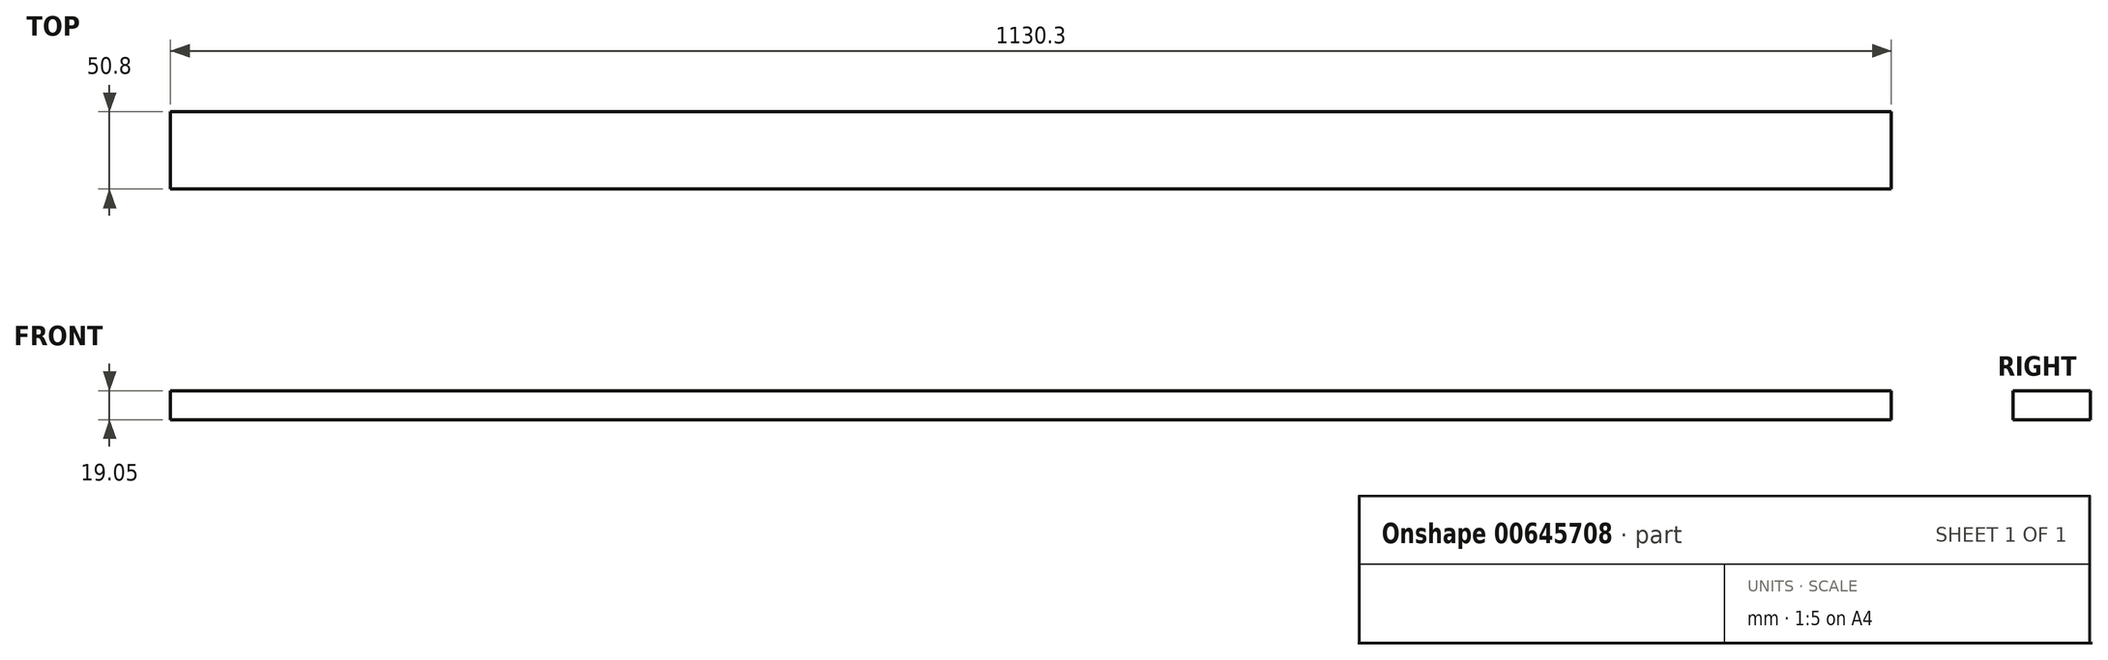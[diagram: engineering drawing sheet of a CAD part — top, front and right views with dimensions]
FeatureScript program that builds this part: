
annotation { "Feature Type Name" : "Feature", "Feature Type Description" : "" }
export const myFeature = defineFeature(function(context is Context, id is Id, definition is map)
    precondition{}
    {
        {
            var Q0;
            Q0=qCreatedBy(makeId("Top.planeOp"),FACE);
            var sketch = newSketch(context, id + "F0", { "sketchPlane" : qUnion([Q0])});
            skLineSegment(sketch, "E0.bottom", {"start": v(-565.15, 25.4) * mm, "end": v(565.15, 25.4) * mm});
            skLineSegment(sketch, "E0.top", {"start": v(-565.15, -25.4) * mm, "end": v(565.15, -25.4) * mm});
            skLineSegment(sketch, "E0.left", {"start": v(-565.15, 25.4) * mm, "end": v(-565.15, -25.4) * mm});
            skLineSegment(sketch, "E0.right", {"start": v(565.15, 25.4) * mm, "end": v(565.15, -25.4) * mm});
            skPoint(sketch, "E0.middle", {"position": v(0, 0) * mm});
            skSolve(sketch);
        }
        {
            var Q0;
            Q0=makeQuery(id+"F0.imprint","IMPRINT",FACE,{"disambiguationData":[TD([[makeQuery(id+"F0.imprint","IMPRINT",EDGE,{"derivedFrom":sQuery(id+"F0.wireOp",EDGE,"E0.bottom")}),-1.0]])]});
            extrude(context, id + "F1", {"entities" : qUnion([Q0]), "depth" : 19.05 * mm, "offsetDistance" : 25.4 * mm});
        }
    });
